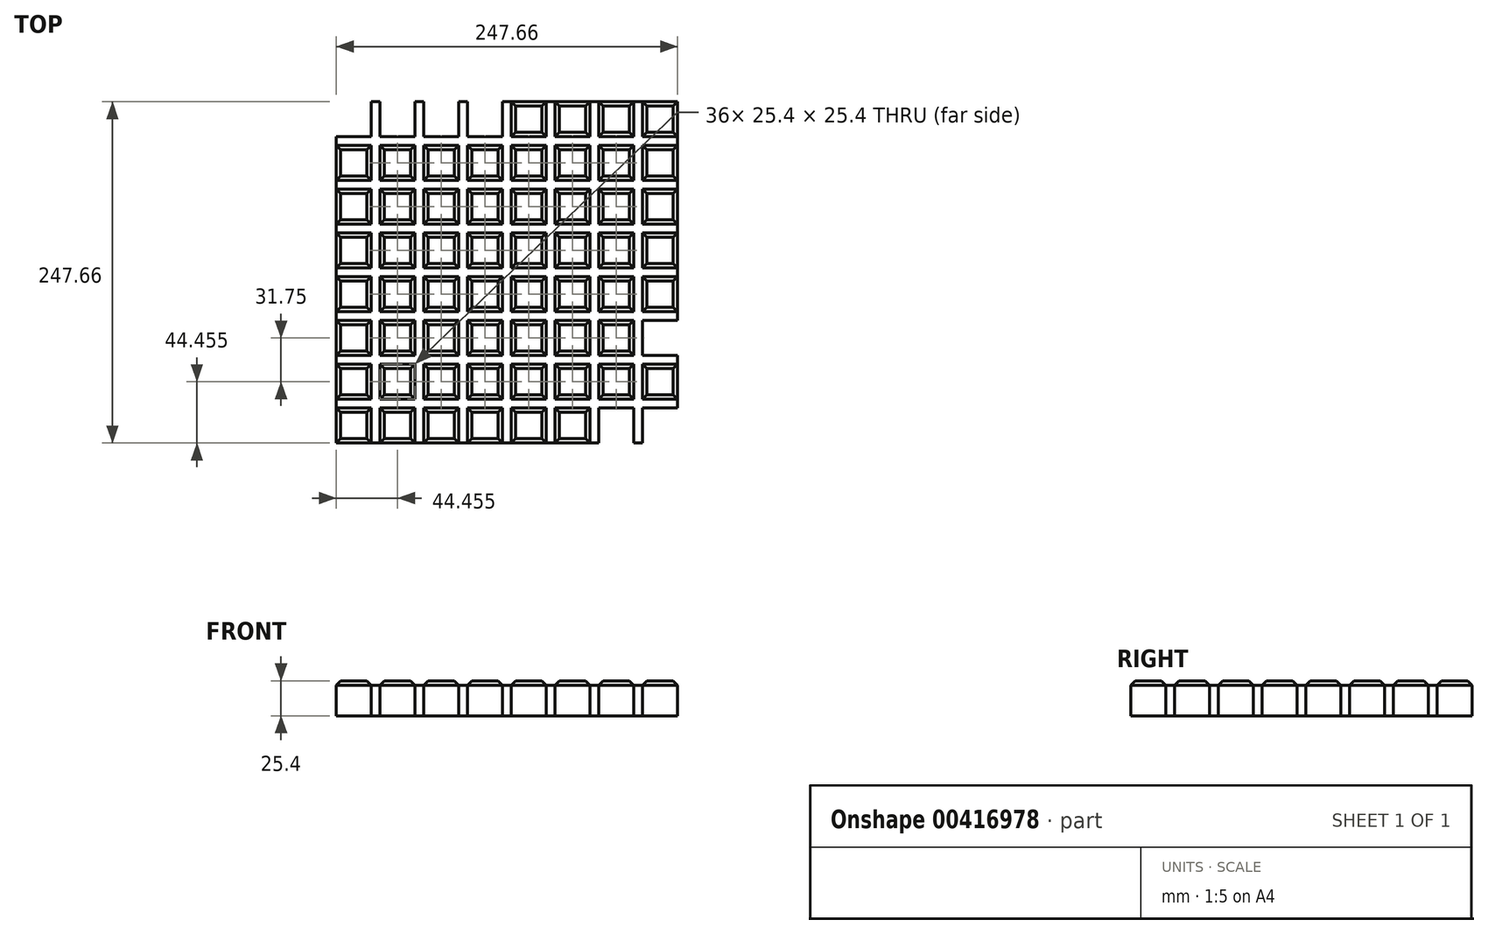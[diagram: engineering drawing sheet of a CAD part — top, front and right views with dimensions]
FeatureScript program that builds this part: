
annotation { "Feature Type Name" : "Feature", "Feature Type Description" : "" }
export const myFeature = defineFeature(function(context is Context, id is Id, definition is map)
    precondition{}
    {
        {
            var Q0;
            Q0=qCreatedBy(makeId("Top.planeOp"),FACE);
            var sketch = newSketch(context, id + "F0", { "sketchPlane" : qUnion([Q0])});
            skLineSegment(sketch, "E0.bottom", {"start": v(123.83, 123.83) * mm, "end": v(-123.83, 123.83) * mm});
            skLineSegment(sketch, "E0.top", {"start": v(123.83, -123.83) * mm, "end": v(-123.83, -123.83) * mm});
            skLineSegment(sketch, "E0.left", {"start": v(123.83, 123.83) * mm, "end": v(123.83, -123.83) * mm});
            skLineSegment(sketch, "E0.right", {"start": v(-123.83, 123.82) * mm, "end": v(-123.83, -123.82) * mm});
            skLineSegment(sketch, "E1.bottom", {"start": v(-123.83, 123.83) * mm, "end": v(-98.43, 123.83) * mm});
            skLineSegment(sketch, "E1.top", {"start": v(-123.83, 98.43) * mm, "end": v(-98.43, 98.43) * mm});
            skLineSegment(sketch, "E1.left", {"start": v(-123.83, 123.83) * mm, "end": v(-123.83, 98.43) * mm});
            skLineSegment(sketch, "E1.right", {"start": v(-98.43, 123.83) * mm, "end": v(-98.43, 98.43) * mm});
            skLineSegment(sketch, "E2.bottom", {"start": v(-123.83, 92.08) * mm, "end": v(-98.43, 92.08) * mm});
            skLineSegment(sketch, "E2.top", {"start": v(-123.83, 66.68) * mm, "end": v(-98.43, 66.68) * mm});
            skLineSegment(sketch, "E2.left", {"start": v(-123.83, 92.08) * mm, "end": v(-123.83, 66.68) * mm});
            skLineSegment(sketch, "E2.right", {"start": v(-98.43, 92.08) * mm, "end": v(-98.43, 66.68) * mm});
            skLineSegment(sketch, "E3.bottom", {"start": v(-92.08, 123.83) * mm, "end": v(-66.68, 123.83) * mm});
            skLineSegment(sketch, "E3.top", {"start": v(-92.08, 98.43) * mm, "end": v(-66.68, 98.43) * mm});
            skLineSegment(sketch, "E3.left", {"start": v(-92.08, 123.83) * mm, "end": v(-92.08, 98.43) * mm});
            skLineSegment(sketch, "E3.right", {"start": v(-66.68, 123.83) * mm, "end": v(-66.68, 98.43) * mm});
            skLineSegment(sketch, "E4.bottom", {"start": v(-123.83, 60.33) * mm, "end": v(-98.43, 60.33) * mm});
            skLineSegment(sketch, "E4.top", {"start": v(-123.83, 34.92) * mm, "end": v(-98.43, 34.92) * mm});
            skLineSegment(sketch, "E4.left", {"start": v(-123.83, 60.33) * mm, "end": v(-123.83, 34.92) * mm});
            skLineSegment(sketch, "E4.right", {"start": v(-98.43, 60.33) * mm, "end": v(-98.43, 34.92) * mm});
            skLineSegment(sketch, "E5.bottom", {"start": v(-60.33, 123.83) * mm, "end": v(-34.93, 123.83) * mm});
            skLineSegment(sketch, "E5.top", {"start": v(-60.33, 98.43) * mm, "end": v(-34.93, 98.43) * mm});
            skLineSegment(sketch, "E5.left", {"start": v(-60.33, 123.83) * mm, "end": v(-60.33, 98.43) * mm});
            skLineSegment(sketch, "E5.right", {"start": v(-34.93, 123.83) * mm, "end": v(-34.93, 98.43) * mm});
            skLineSegment(sketch, "E6.bottom", {"start": v(-92.08, 92.08) * mm, "end": v(-66.68, 92.08) * mm});
            skLineSegment(sketch, "E6.top", {"start": v(-92.08, 66.68) * mm, "end": v(-66.68, 66.68) * mm});
            skLineSegment(sketch, "E6.left", {"start": v(-92.08, 92.08) * mm, "end": v(-92.08, 66.68) * mm});
            skLineSegment(sketch, "E6.right", {"start": v(-66.68, 92.08) * mm, "end": v(-66.68, 66.68) * mm});
            skLineSegment(sketch, "E7.bottom", {"start": v(-92.08, 60.33) * mm, "end": v(-66.68, 60.33) * mm});
            skLineSegment(sketch, "E7.top", {"start": v(-92.08, 34.93) * mm, "end": v(-66.68, 34.93) * mm});
            skLineSegment(sketch, "E7.left", {"start": v(-92.08, 60.33) * mm, "end": v(-92.08, 34.93) * mm});
            skLineSegment(sketch, "E7.right", {"start": v(-66.68, 60.33) * mm, "end": v(-66.68, 34.93) * mm});
            skLineSegment(sketch, "E8.bottom", {"start": v(-60.33, 92.08) * mm, "end": v(-34.93, 92.08) * mm});
            skLineSegment(sketch, "E8.top", {"start": v(-60.33, 66.68) * mm, "end": v(-34.93, 66.68) * mm});
            skLineSegment(sketch, "E8.left", {"start": v(-60.33, 92.08) * mm, "end": v(-60.33, 66.68) * mm});
            skLineSegment(sketch, "E8.right", {"start": v(-34.93, 92.08) * mm, "end": v(-34.93, 66.68) * mm});
            skLineSegment(sketch, "E9.bottom", {"start": v(-60.33, 60.33) * mm, "end": v(-34.93, 60.33) * mm});
            skLineSegment(sketch, "E9.top", {"start": v(-60.33, 34.93) * mm, "end": v(-34.93, 34.93) * mm});
            skLineSegment(sketch, "E9.left", {"start": v(-60.33, 60.33) * mm, "end": v(-60.33, 34.93) * mm});
            skLineSegment(sketch, "E9.right", {"start": v(-34.93, 60.33) * mm, "end": v(-34.93, 34.93) * mm});
            skLineSegment(sketch, "E10.bottom", {"start": v(-60.33, 28.58) * mm, "end": v(-34.93, 28.58) * mm});
            skLineSegment(sketch, "E10.top", {"start": v(-60.33, 3.18) * mm, "end": v(-34.93, 3.18) * mm});
            skLineSegment(sketch, "E10.left", {"start": v(-60.33, 28.58) * mm, "end": v(-60.33, 3.18) * mm});
            skLineSegment(sketch, "E10.right", {"start": v(-34.93, 28.58) * mm, "end": v(-34.93, 3.18) * mm});
            skLineSegment(sketch, "E11.bottom", {"start": v(-92.08, 28.58) * mm, "end": v(-66.68, 28.58) * mm});
            skLineSegment(sketch, "E11.top", {"start": v(-92.08, 3.18) * mm, "end": v(-66.68, 3.18) * mm});
            skLineSegment(sketch, "E11.left", {"start": v(-92.08, 28.58) * mm, "end": v(-92.08, 3.18) * mm});
            skLineSegment(sketch, "E11.right", {"start": v(-66.68, 28.58) * mm, "end": v(-66.68, 3.18) * mm});
            skLineSegment(sketch, "E12.bottom", {"start": v(-123.83, 28.58) * mm, "end": v(-98.43, 28.58) * mm});
            skLineSegment(sketch, "E12.top", {"start": v(-123.83, 3.18) * mm, "end": v(-98.43, 3.18) * mm});
            skLineSegment(sketch, "E12.left", {"start": v(-123.83, 28.58) * mm, "end": v(-123.83, 3.18) * mm});
            skLineSegment(sketch, "E12.right", {"start": v(-98.43, 28.58) * mm, "end": v(-98.43, 3.18) * mm});
            skLineSegment(sketch, "E13.bottom", {"start": v(-28.58, 123.83) * mm, "end": v(-3.18, 123.83) * mm});
            skLineSegment(sketch, "E13.top", {"start": v(-28.58, 98.43) * mm, "end": v(-3.18, 98.43) * mm});
            skLineSegment(sketch, "E13.left", {"start": v(-28.58, 123.83) * mm, "end": v(-28.58, 98.42) * mm});
            skLineSegment(sketch, "E13.right", {"start": v(-3.18, 123.83) * mm, "end": v(-3.18, 98.42) * mm});
            skLineSegment(sketch, "E14.bottom", {"start": v(-28.58, 92.07) * mm, "end": v(-3.18, 92.07) * mm});
            skLineSegment(sketch, "E14.top", {"start": v(-28.58, 66.67) * mm, "end": v(-3.18, 66.67) * mm});
            skLineSegment(sketch, "E14.left", {"start": v(-28.58, 92.07) * mm, "end": v(-28.58, 66.67) * mm});
            skLineSegment(sketch, "E14.right", {"start": v(-3.18, 92.08) * mm, "end": v(-3.18, 66.67) * mm});
            skLineSegment(sketch, "E15.bottom", {"start": v(-28.58, 60.32) * mm, "end": v(-3.18, 60.32) * mm});
            skLineSegment(sketch, "E15.top", {"start": v(-28.58, 34.92) * mm, "end": v(-3.18, 34.92) * mm});
            skLineSegment(sketch, "E15.left", {"start": v(-28.58, 60.32) * mm, "end": v(-28.58, 34.92) * mm});
            skLineSegment(sketch, "E15.right", {"start": v(-3.18, 60.32) * mm, "end": v(-3.18, 34.92) * mm});
            skLineSegment(sketch, "E16.bottom", {"start": v(-28.58, 28.57) * mm, "end": v(-3.18, 28.57) * mm});
            skLineSegment(sketch, "E16.top", {"start": v(-28.58, 3.17) * mm, "end": v(-3.18, 3.17) * mm});
            skLineSegment(sketch, "E16.left", {"start": v(-28.58, 28.57) * mm, "end": v(-28.58, 3.17) * mm});
            skLineSegment(sketch, "E16.right", {"start": v(-3.18, 28.57) * mm, "end": v(-3.18, 3.17) * mm});
            skLineSegment(sketch, "E17.MirrorCS", {"start": v(28.57, 60.32) * mm, "end": v(28.57, 34.92) * mm});
            skLineSegment(sketch, "E18.MirrorCS", {"start": v(60.33, 34.93) * mm, "end": v(34.93, 34.93) * mm});
            skLineSegment(sketch, "E19.MirrorCS", {"start": v(60.32, 60.33) * mm, "end": v(60.32, 34.93) * mm});
            skLineSegment(sketch, "E20.MirrorCS", {"start": v(60.33, 28.58) * mm, "end": v(34.93, 28.58) * mm});
            skLineSegment(sketch, "E21.MirrorCS", {"start": v(92.08, 98.43) * mm, "end": v(66.68, 98.43) * mm});
            skLineSegment(sketch, "E22.MirrorCS", {"start": v(66.67, 28.57) * mm, "end": v(66.67, 3.17) * mm});
            skLineSegment(sketch, "E23.MirrorCS", {"start": v(28.58, 60.33) * mm, "end": v(3.18, 60.33) * mm});
            skLineSegment(sketch, "E24.MirrorCS", {"start": v(60.32, 28.58) * mm, "end": v(60.33, 3.17) * mm});
            skLineSegment(sketch, "E25.MirrorCS", {"start": v(92.08, 28.58) * mm, "end": v(66.68, 28.58) * mm});
            skLineSegment(sketch, "E26.MirrorCS", {"start": v(98.42, 92.08) * mm, "end": v(98.42, 66.67) * mm});
            skLineSegment(sketch, "E27.MirrorCS", {"start": v(92.08, 92.08) * mm, "end": v(66.68, 92.08) * mm});
            skLineSegment(sketch, "E28.MirrorCS", {"start": v(92.07, 28.57) * mm, "end": v(92.08, 3.17) * mm});
            skLineSegment(sketch, "E29.MirrorCS", {"start": v(98.42, 60.32) * mm, "end": v(98.42, 34.92) * mm});
            skLineSegment(sketch, "E30.MirrorCS", {"start": v(34.92, 60.33) * mm, "end": v(34.92, 34.93) * mm});
            skLineSegment(sketch, "E31.MirrorCS", {"start": v(98.42, 28.57) * mm, "end": v(98.42, 3.17) * mm});
            skLineSegment(sketch, "E32.MirrorCS", {"start": v(28.57, 92.07) * mm, "end": v(28.57, 66.67) * mm});
            skLineSegment(sketch, "E33.MirrorCS", {"start": v(98.42, 123.83) * mm, "end": v(98.42, 98.43) * mm});
            skLineSegment(sketch, "E34.MirrorCS", {"start": v(123.83, 92.08) * mm, "end": v(98.43, 92.08) * mm});
            skLineSegment(sketch, "E35.MirrorCS", {"start": v(28.58, 28.58) * mm, "end": v(3.18, 28.58) * mm});
            skLineSegment(sketch, "E36.MirrorCS", {"start": v(92.07, 92.07) * mm, "end": v(92.07, 66.67) * mm});
            skLineSegment(sketch, "E37.MirrorCS", {"start": v(66.67, 92.08) * mm, "end": v(66.67, 66.68) * mm});
            skLineSegment(sketch, "E38.MirrorCS", {"start": v(92.07, 60.32) * mm, "end": v(92.07, 34.92) * mm});
            skLineSegment(sketch, "E39.MirrorCS", {"start": v(28.57, 123.83) * mm, "end": v(28.57, 98.42) * mm});
            skLineSegment(sketch, "E40.MirrorCS", {"start": v(66.67, 60.33) * mm, "end": v(66.67, 34.93) * mm});
            skLineSegment(sketch, "E41.MirrorCS", {"start": v(92.07, 123.82) * mm, "end": v(92.07, 98.42) * mm});
            skLineSegment(sketch, "E42.MirrorCS", {"start": v(28.58, 66.68) * mm, "end": v(3.18, 66.68) * mm});
            skLineSegment(sketch, "E43.MirrorCS", {"start": v(34.92, 92.08) * mm, "end": v(34.92, 66.68) * mm});
            skLineSegment(sketch, "E44.MirrorCS", {"start": v(60.32, 92.08) * mm, "end": v(60.32, 66.68) * mm});
            skLineSegment(sketch, "E45.MirrorCS", {"start": v(123.83, 98.43) * mm, "end": v(98.43, 98.43) * mm});
            skLineSegment(sketch, "E46.MirrorCS", {"start": v(28.58, 34.93) * mm, "end": v(3.18, 34.93) * mm});
            skLineSegment(sketch, "E47.MirrorCS", {"start": v(92.08, 34.93) * mm, "end": v(66.68, 34.93) * mm});
            skLineSegment(sketch, "E48.MirrorCS", {"start": v(34.92, 123.83) * mm, "end": v(34.92, 98.43) * mm});
            skLineSegment(sketch, "E49.MirrorCS", {"start": v(28.58, 28.57) * mm, "end": v(28.58, 3.17) * mm});
            skLineSegment(sketch, "E50.MirrorCS", {"start": v(123.83, 28.57) * mm, "end": v(123.83, 3.17) * mm});
            skLineSegment(sketch, "E51.MirrorCS", {"start": v(92.08, 60.33) * mm, "end": v(66.68, 60.33) * mm});
            skLineSegment(sketch, "E52.MirrorCS", {"start": v(60.33, 98.43) * mm, "end": v(34.93, 98.43) * mm});
            skLineSegment(sketch, "E53.MirrorCS", {"start": v(92.08, 66.68) * mm, "end": v(66.68, 66.68) * mm});
            skLineSegment(sketch, "E54.MirrorCS", {"start": v(3.17, 60.32) * mm, "end": v(3.17, 34.92) * mm});
            skLineSegment(sketch, "E55.MirrorCS", {"start": v(92.08, 123.83) * mm, "end": v(66.68, 123.83) * mm});
            skLineSegment(sketch, "E56.MirrorCS", {"start": v(28.58, 98.43) * mm, "end": v(3.18, 98.43) * mm});
            skLineSegment(sketch, "E57.MirrorCS", {"start": v(123.82, 60.32) * mm, "end": v(123.82, 34.92) * mm});
            skLineSegment(sketch, "E58.MirrorCS", {"start": v(28.58, 3.18) * mm, "end": v(3.18, 3.18) * mm});
            skLineSegment(sketch, "E59.MirrorCS", {"start": v(123.83, 66.68) * mm, "end": v(98.43, 66.68) * mm});
            skLineSegment(sketch, "E60.MirrorCS", {"start": v(123.83, 28.58) * mm, "end": v(98.43, 28.58) * mm});
            skLineSegment(sketch, "E61.MirrorCS", {"start": v(60.33, 66.68) * mm, "end": v(34.93, 66.68) * mm});
            skLineSegment(sketch, "E62.MirrorCS", {"start": v(60.33, 92.08) * mm, "end": v(34.93, 92.08) * mm});
            skLineSegment(sketch, "E63.MirrorCS", {"start": v(28.58, 123.83) * mm, "end": v(3.18, 123.83) * mm});
            skLineSegment(sketch, "E64.MirrorCS", {"start": v(92.08, 3.18) * mm, "end": v(66.68, 3.18) * mm});
            skLineSegment(sketch, "E65.MirrorCS", {"start": v(60.33, 3.18) * mm, "end": v(34.93, 3.18) * mm});
            skLineSegment(sketch, "E66.MirrorCS", {"start": v(28.58, 92.08) * mm, "end": v(3.18, 92.08) * mm});
            skLineSegment(sketch, "E67.MirrorCS", {"start": v(60.32, 123.83) * mm, "end": v(60.32, 98.43) * mm});
            skLineSegment(sketch, "E68.MirrorCS", {"start": v(66.67, 123.82) * mm, "end": v(66.67, 98.43) * mm});
            skLineSegment(sketch, "E69.MirrorCS", {"start": v(123.83, 123.83) * mm, "end": v(98.43, 123.83) * mm});
            skLineSegment(sketch, "E70.MirrorCS", {"start": v(3.18, 28.57) * mm, "end": v(3.18, 3.17) * mm});
            skLineSegment(sketch, "E71.MirrorCS", {"start": v(34.93, 28.58) * mm, "end": v(34.93, 3.18) * mm});
            skLineSegment(sketch, "E72.MirrorCS", {"start": v(3.17, 92.08) * mm, "end": v(3.17, 66.67) * mm});
            skLineSegment(sketch, "E73.MirrorCS", {"start": v(123.83, 123.82) * mm, "end": v(123.83, 98.42) * mm});
            skLineSegment(sketch, "E74.MirrorCS", {"start": v(123.83, 34.93) * mm, "end": v(98.43, 34.93) * mm});
            skLineSegment(sketch, "E75.MirrorCS", {"start": v(60.33, 123.83) * mm, "end": v(34.93, 123.83) * mm});
            skLineSegment(sketch, "E76.MirrorCS", {"start": v(123.82, 92.07) * mm, "end": v(123.82, 66.67) * mm});
            skLineSegment(sketch, "E77.MirrorCS", {"start": v(60.33, 60.33) * mm, "end": v(34.93, 60.33) * mm});
            skLineSegment(sketch, "E78.MirrorCS", {"start": v(123.83, 3.18) * mm, "end": v(98.43, 3.18) * mm});
            skLineSegment(sketch, "E79.MirrorCS", {"start": v(3.17, 123.83) * mm, "end": v(3.17, 98.42) * mm});
            skLineSegment(sketch, "E80.MirrorCS", {"start": v(123.83, 60.33) * mm, "end": v(98.43, 60.33) * mm});
            skLineSegment(sketch, "E81.MirrorCS", {"start": v(-60.32, -60.33) * mm, "end": v(-60.32, -34.93) * mm});
            skLineSegment(sketch, "E82.MirrorCS", {"start": v(-92.08, -28.58) * mm, "end": v(-66.68, -28.58) * mm});
            skLineSegment(sketch, "E83.MirrorCS", {"start": v(-92.08, -60.33) * mm, "end": v(-66.68, -60.33) * mm});
            skLineSegment(sketch, "E84.MirrorCS", {"start": v(-92.07, -92.08) * mm, "end": v(-92.07, -66.68) * mm});
            skLineSegment(sketch, "E85.MirrorCS", {"start": v(-28.58, -28.57) * mm, "end": v(-3.18, -28.57) * mm});
            skLineSegment(sketch, "E86.MirrorCS", {"start": v(-123.83, -60.33) * mm, "end": v(-98.43, -60.33) * mm});
            skLineSegment(sketch, "E87.MirrorCS", {"start": v(-28.58, -60.33) * mm, "end": v(-3.18, -60.33) * mm});
            skLineSegment(sketch, "E88.MirrorCS", {"start": v(-123.83, -66.68) * mm, "end": v(-98.43, -66.68) * mm});
            skLineSegment(sketch, "E89.MirrorCS", {"start": v(-60.33, -34.93) * mm, "end": v(-34.93, -34.93) * mm});
            skLineSegment(sketch, "E90.MirrorCS", {"start": v(-60.33, -92.08) * mm, "end": v(-34.93, -92.08) * mm});
            skLineSegment(sketch, "E91.MirrorCS", {"start": v(-60.32, -92.08) * mm, "end": v(-60.32, -66.68) * mm});
            skLineSegment(sketch, "E92.MirrorCS", {"start": v(-28.58, -98.43) * mm, "end": v(-3.17, -98.43) * mm});
            skLineSegment(sketch, "E93.MirrorCS", {"start": v(-28.57, -123.83) * mm, "end": v(-28.57, -98.42) * mm});
            skLineSegment(sketch, "E94.MirrorCS", {"start": v(-98.42, -123.83) * mm, "end": v(-98.42, -98.43) * mm});
            skLineSegment(sketch, "E95.MirrorCS", {"start": v(-123.83, -92.08) * mm, "end": v(-98.43, -92.08) * mm});
            skLineSegment(sketch, "E96.MirrorCS", {"start": v(-60.33, -98.43) * mm, "end": v(-34.93, -98.43) * mm});
            skLineSegment(sketch, "E97.MirrorCS", {"start": v(3.18, -123.83) * mm, "end": v(3.18, -98.42) * mm});
            skLineSegment(sketch, "E98.MirrorCS", {"start": v(-66.67, -92.08) * mm, "end": v(-66.67, -66.68) * mm});
            skLineSegment(sketch, "E99.MirrorCS", {"start": v(-60.33, -28.58) * mm, "end": v(-34.93, -28.58) * mm});
            skLineSegment(sketch, "E100.MirrorCS", {"start": v(-28.58, -92.08) * mm, "end": v(-3.18, -92.08) * mm});
            skLineSegment(sketch, "E101.MirrorCS", {"start": v(-98.43, -92.08) * mm, "end": v(-98.43, -66.68) * mm});
            skLineSegment(sketch, "E102.MirrorCS", {"start": v(-123.83, -98.43) * mm, "end": v(-98.43, -98.43) * mm});
            skLineSegment(sketch, "E103.MirrorCS", {"start": v(-98.42, -28.58) * mm, "end": v(-98.43, -3.18) * mm});
            skLineSegment(sketch, "E104.MirrorCS", {"start": v(-92.07, -123.83) * mm, "end": v(-92.07, -98.43) * mm});
            skLineSegment(sketch, "E105.MirrorCS", {"start": v(-92.08, -98.43) * mm, "end": v(-66.68, -98.43) * mm});
            skLineSegment(sketch, "E106.MirrorCS", {"start": v(-28.58, -66.68) * mm, "end": v(-3.17, -66.68) * mm});
            skLineSegment(sketch, "E107.MirrorCS", {"start": v(-66.67, -60.33) * mm, "end": v(-66.67, -34.93) * mm});
            skLineSegment(sketch, "E108.MirrorCS", {"start": v(-66.67, -28.58) * mm, "end": v(-66.68, -3.18) * mm});
            skLineSegment(sketch, "E109.MirrorCS", {"start": v(-92.08, -92.08) * mm, "end": v(-66.68, -92.08) * mm});
            skLineSegment(sketch, "E110.MirrorCS", {"start": v(-92.08, -34.93) * mm, "end": v(-66.68, -34.93) * mm});
            skLineSegment(sketch, "E111.MirrorCS", {"start": v(-28.58, -34.93) * mm, "end": v(-3.18, -34.93) * mm});
            skLineSegment(sketch, "E112.MirrorCS", {"start": v(-34.92, -92.08) * mm, "end": v(-34.92, -66.68) * mm});
            skLineSegment(sketch, "E113.MirrorCS", {"start": v(-34.92, -123.83) * mm, "end": v(-34.92, -98.43) * mm});
            skLineSegment(sketch, "E114.MirrorCS", {"start": v(-34.92, -60.33) * mm, "end": v(-34.92, -34.93) * mm});
            skLineSegment(sketch, "E115.MirrorCS", {"start": v(-3.17, -123.83) * mm, "end": v(-3.17, -98.42) * mm});
            skLineSegment(sketch, "E116.MirrorCS", {"start": v(-60.32, -28.58) * mm, "end": v(-60.33, -3.18) * mm});
            skLineSegment(sketch, "E117.MirrorCS", {"start": v(-28.57, -92.07) * mm, "end": v(-28.57, -66.67) * mm});
            skLineSegment(sketch, "E118.MirrorCS", {"start": v(-98.43, -60.33) * mm, "end": v(-98.43, -34.93) * mm});
            skLineSegment(sketch, "E119.MirrorCS", {"start": v(-28.57, -60.32) * mm, "end": v(-28.57, -34.92) * mm});
            skLineSegment(sketch, "E120.MirrorCS", {"start": v(-92.07, -28.58) * mm, "end": v(-92.08, -3.18) * mm});
            skLineSegment(sketch, "E121.MirrorCS", {"start": v(-92.07, -60.33) * mm, "end": v(-92.07, -34.93) * mm});
            skLineSegment(sketch, "E122.MirrorCS", {"start": v(28.58, -28.57) * mm, "end": v(28.58, -3.17) * mm});
            skLineSegment(sketch, "E123.MirrorCS", {"start": v(28.58, -28.58) * mm, "end": v(3.18, -28.58) * mm});
            skLineSegment(sketch, "E124.MirrorCS", {"start": v(-123.83, -92.08) * mm, "end": v(-123.83, -66.68) * mm});
            skLineSegment(sketch, "E125.MirrorCS", {"start": v(-92.08, -66.68) * mm, "end": v(-66.68, -66.68) * mm});
            skLineSegment(sketch, "E126.MirrorCS", {"start": v(-28.57, -123.83) * mm, "end": v(-3.17, -123.83) * mm});
            skLineSegment(sketch, "E127.MirrorCS", {"start": v(28.58, -60.33) * mm, "end": v(3.18, -60.33) * mm});
            skLineSegment(sketch, "E128.MirrorCS", {"start": v(-123.83, -60.33) * mm, "end": v(-123.83, -34.93) * mm});
            skLineSegment(sketch, "E129.MirrorCS", {"start": v(28.58, -123.83) * mm, "end": v(28.58, -98.42) * mm});
            skLineSegment(sketch, "E130.MirrorCS", {"start": v(-123.83, -28.58) * mm, "end": v(-98.43, -28.58) * mm});
            skLineSegment(sketch, "E131.MirrorCS", {"start": v(-123.83, -34.93) * mm, "end": v(-98.43, -34.93) * mm});
            skLineSegment(sketch, "E132.MirrorCS", {"start": v(-60.32, -123.83) * mm, "end": v(-60.32, -98.43) * mm});
            skLineSegment(sketch, "E133.MirrorCS", {"start": v(-60.33, -123.83) * mm, "end": v(-34.93, -123.83) * mm});
            skLineSegment(sketch, "E134.MirrorCS", {"start": v(3.18, -60.32) * mm, "end": v(3.18, -34.92) * mm});
            skLineSegment(sketch, "E135.MirrorCS", {"start": v(28.58, -123.83) * mm, "end": v(3.18, -123.83) * mm});
            skLineSegment(sketch, "E136.MirrorCS", {"start": v(-123.83, -28.58) * mm, "end": v(-123.83, -3.18) * mm});
            skLineSegment(sketch, "E137.MirrorCS", {"start": v(28.58, -60.32) * mm, "end": v(28.58, -34.92) * mm});
            skLineSegment(sketch, "E138.MirrorCS", {"start": v(-92.08, -123.83) * mm, "end": v(-66.68, -123.83) * mm});
            skLineSegment(sketch, "E139.MirrorCS", {"start": v(-28.57, -28.57) * mm, "end": v(-28.58, -3.17) * mm});
            skLineSegment(sketch, "E140.MirrorCS", {"start": v(-60.33, -66.68) * mm, "end": v(-34.93, -66.68) * mm});
            skLineSegment(sketch, "E141.MirrorCS", {"start": v(28.58, -34.93) * mm, "end": v(3.18, -34.93) * mm});
            skLineSegment(sketch, "E142.MirrorCS", {"start": v(-3.17, -92.08) * mm, "end": v(-3.17, -66.67) * mm});
            skLineSegment(sketch, "E143.MirrorCS", {"start": v(-123.83, -123.83) * mm, "end": v(-123.83, -98.43) * mm});
            skLineSegment(sketch, "E144.MirrorCS", {"start": v(-123.83, -3.18) * mm, "end": v(-98.43, -3.18) * mm});
            skLineSegment(sketch, "E145.MirrorCS", {"start": v(-28.58, -3.17) * mm, "end": v(-3.18, -3.17) * mm});
            skLineSegment(sketch, "E146.MirrorCS", {"start": v(-123.83, -123.83) * mm, "end": v(-98.43, -123.83) * mm});
            skLineSegment(sketch, "E147.MirrorCS", {"start": v(-66.67, -123.83) * mm, "end": v(-66.67, -98.43) * mm});
            skLineSegment(sketch, "E148.MirrorCS", {"start": v(28.58, -66.67) * mm, "end": v(3.18, -66.68) * mm});
            skLineSegment(sketch, "E149.MirrorCS", {"start": v(28.58, -3.18) * mm, "end": v(3.18, -3.18) * mm});
            skLineSegment(sketch, "E150.MirrorCS", {"start": v(-3.17, -60.32) * mm, "end": v(-3.17, -34.92) * mm});
            skLineSegment(sketch, "E151.MirrorCS", {"start": v(-60.33, -3.18) * mm, "end": v(-34.93, -3.18) * mm});
            skLineSegment(sketch, "E152.MirrorCS", {"start": v(28.58, -92.07) * mm, "end": v(28.58, -66.67) * mm});
            skLineSegment(sketch, "E153.MirrorCS", {"start": v(-92.08, -3.18) * mm, "end": v(-66.68, -3.18) * mm});
            skLineSegment(sketch, "E154.MirrorCS", {"start": v(3.18, -28.57) * mm, "end": v(3.18, -3.17) * mm});
            skLineSegment(sketch, "E155.MirrorCS", {"start": v(-34.93, -28.58) * mm, "end": v(-34.93, -3.18) * mm});
            skLineSegment(sketch, "E156.MirrorCS", {"start": v(-60.33, -60.33) * mm, "end": v(-34.93, -60.33) * mm});
            skLineSegment(sketch, "E157.MirrorCS", {"start": v(28.58, -92.08) * mm, "end": v(3.18, -92.08) * mm});
            skLineSegment(sketch, "E158.MirrorCS", {"start": v(3.18, -92.08) * mm, "end": v(3.18, -66.67) * mm});
            skLineSegment(sketch, "E159.MirrorCS", {"start": v(-3.17, -28.57) * mm, "end": v(-3.18, -3.17) * mm});
            skLineSegment(sketch, "E160.MirrorCS", {"start": v(28.58, -98.42) * mm, "end": v(3.18, -98.43) * mm});
            skLineSegment(sketch, "E161.MirrorCS", {"start": v(66.68, -60.33) * mm, "end": v(66.68, -34.92) * mm});
            skLineSegment(sketch, "E162.MirrorCS", {"start": v(60.33, -92.08) * mm, "end": v(34.93, -92.08) * mm});
            skLineSegment(sketch, "E163.MirrorCS", {"start": v(92.08, -60.32) * mm, "end": v(92.08, -34.92) * mm});
            skLineSegment(sketch, "E164.MirrorCS", {"start": v(92.08, -123.83) * mm, "end": v(66.68, -123.83) * mm});
            skLineSegment(sketch, "E165.MirrorCS", {"start": v(123.83, -3.17) * mm, "end": v(98.43, -3.17) * mm});
            skLineSegment(sketch, "E166.MirrorCS", {"start": v(92.08, -28.57) * mm, "end": v(66.68, -28.57) * mm});
            skLineSegment(sketch, "E167.MirrorCS", {"start": v(92.08, -123.82) * mm, "end": v(92.08, -98.42) * mm});
            skLineSegment(sketch, "E168.MirrorCS", {"start": v(123.83, -60.32) * mm, "end": v(123.83, -34.92) * mm});
            skLineSegment(sketch, "E169.MirrorCS", {"start": v(66.68, -28.57) * mm, "end": v(66.68, -3.17) * mm});
            skLineSegment(sketch, "E170.MirrorCS", {"start": v(34.93, -28.58) * mm, "end": v(34.93, -3.18) * mm});
            skLineSegment(sketch, "E171.MirrorCS", {"start": v(123.83, -123.82) * mm, "end": v(123.83, -98.42) * mm});
            skLineSegment(sketch, "E172.MirrorCS", {"start": v(123.83, -92.07) * mm, "end": v(98.43, -92.07) * mm});
            skLineSegment(sketch, "E173.MirrorCS", {"start": v(92.08, -34.92) * mm, "end": v(66.68, -34.93) * mm});
            skLineSegment(sketch, "E174.MirrorCS", {"start": v(98.43, -28.57) * mm, "end": v(98.43, -3.17) * mm});
            skLineSegment(sketch, "E175.MirrorCS", {"start": v(34.93, -60.33) * mm, "end": v(34.93, -34.93) * mm});
            skLineSegment(sketch, "E176.MirrorCS", {"start": v(60.33, -98.42) * mm, "end": v(34.93, -98.42) * mm});
            skLineSegment(sketch, "E177.MirrorCS", {"start": v(92.08, -92.07) * mm, "end": v(92.08, -66.67) * mm});
            skLineSegment(sketch, "E178.MirrorCS", {"start": v(123.83, -60.32) * mm, "end": v(98.43, -60.32) * mm});
            skLineSegment(sketch, "E179.MirrorCS", {"start": v(92.08, -60.32) * mm, "end": v(66.68, -60.32) * mm});
            skLineSegment(sketch, "E180.MirrorCS", {"start": v(92.08, -3.17) * mm, "end": v(66.68, -3.17) * mm});
            skLineSegment(sketch, "E181.MirrorCS", {"start": v(34.93, -123.83) * mm, "end": v(34.93, -98.43) * mm});
            skLineSegment(sketch, "E182.MirrorCS", {"start": v(60.33, -28.58) * mm, "end": v(34.93, -28.58) * mm});
            skLineSegment(sketch, "E183.MirrorCS", {"start": v(98.43, -123.82) * mm, "end": v(98.43, -98.43) * mm});
            skLineSegment(sketch, "E184.MirrorCS", {"start": v(66.68, -123.82) * mm, "end": v(66.68, -98.42) * mm});
            skLineSegment(sketch, "E185.MirrorCS", {"start": v(123.83, -28.57) * mm, "end": v(123.83, -3.17) * mm});
            skLineSegment(sketch, "E186.MirrorCS", {"start": v(60.33, -34.93) * mm, "end": v(34.93, -34.93) * mm});
            skLineSegment(sketch, "E187.MirrorCS", {"start": v(123.83, -123.82) * mm, "end": v(98.43, -123.83) * mm});
            skLineSegment(sketch, "E188.MirrorCS", {"start": v(66.68, -92.08) * mm, "end": v(66.68, -66.68) * mm});
            skLineSegment(sketch, "E189.MirrorCS", {"start": v(92.08, -66.67) * mm, "end": v(66.68, -66.67) * mm});
            skLineSegment(sketch, "E190.MirrorCS", {"start": v(92.08, -98.42) * mm, "end": v(66.68, -98.42) * mm});
            skLineSegment(sketch, "E191.MirrorCS", {"start": v(60.33, -28.57) * mm, "end": v(60.33, -3.17) * mm});
            skLineSegment(sketch, "E192.MirrorCS", {"start": v(60.33, -123.83) * mm, "end": v(60.33, -98.43) * mm});
            skLineSegment(sketch, "E193.MirrorCS", {"start": v(60.33, -60.33) * mm, "end": v(60.33, -34.92) * mm});
            skLineSegment(sketch, "E194.MirrorCS", {"start": v(60.33, -3.17) * mm, "end": v(34.93, -3.17) * mm});
            skLineSegment(sketch, "E195.MirrorCS", {"start": v(98.43, -92.07) * mm, "end": v(98.43, -66.67) * mm});
            skLineSegment(sketch, "E196.MirrorCS", {"start": v(123.83, -34.92) * mm, "end": v(98.43, -34.92) * mm});
            skLineSegment(sketch, "E197.MirrorCS", {"start": v(60.33, -123.83) * mm, "end": v(34.93, -123.83) * mm});
            skLineSegment(sketch, "E198.MirrorCS", {"start": v(123.83, -66.67) * mm, "end": v(98.43, -66.67) * mm});
            skLineSegment(sketch, "E199.MirrorCS", {"start": v(34.93, -92.08) * mm, "end": v(34.93, -66.68) * mm});
            skLineSegment(sketch, "E200.MirrorCS", {"start": v(92.08, -92.07) * mm, "end": v(66.68, -92.08) * mm});
            skLineSegment(sketch, "E201.MirrorCS", {"start": v(92.08, -28.57) * mm, "end": v(92.08, -3.17) * mm});
            skLineSegment(sketch, "E202.MirrorCS", {"start": v(123.83, -92.07) * mm, "end": v(123.83, -66.67) * mm});
            skLineSegment(sketch, "E203.MirrorCS", {"start": v(123.83, -28.57) * mm, "end": v(98.43, -28.57) * mm});
            skLineSegment(sketch, "E204.MirrorCS", {"start": v(60.33, -92.08) * mm, "end": v(60.33, -66.68) * mm});
            skLineSegment(sketch, "E205.MirrorCS", {"start": v(98.43, -60.32) * mm, "end": v(98.43, -34.92) * mm});
            skLineSegment(sketch, "E206.MirrorCS", {"start": v(60.33, -60.33) * mm, "end": v(34.93, -60.33) * mm});
            skLineSegment(sketch, "E207.MirrorCS", {"start": v(123.83, -98.42) * mm, "end": v(98.43, -98.42) * mm});
            skLineSegment(sketch, "E208.MirrorCS", {"start": v(60.33, -66.68) * mm, "end": v(34.93, -66.68) * mm});
            skLineSegment(sketch, "E209.bottom", {"start": v(-130.17, 130.18) * mm, "end": v(130.18, 130.18) * mm});
            skLineSegment(sketch, "E209.top", {"start": v(-130.18, -130.18) * mm, "end": v(130.18, -130.18) * mm});
            skLineSegment(sketch, "E209.left", {"start": v(-130.17, 130.18) * mm, "end": v(-130.18, -130.18) * mm});
            skLineSegment(sketch, "E209.right", {"start": v(130.18, 130.18) * mm, "end": v(130.18, -130.18) * mm});
            skPoint(sketch, "E209.middle", {"position": v(0, 0) * mm});
            skSolve(sketch);
        }
        {
            var Q0;
            Q0=makeQuery(id+"F0.imprint","IMPRINT",FACE,{"disambiguationData":[TD([[makeQuery(id+"F0.imprint","IMPRINT",EDGE,{"derivedFrom":sQuery(id+"F0.wireOp",EDGE,"E32.MirrorCS")}),-1.0]])]});
            var Q1;
            Q1=makeQuery(id+"F0.imprint","IMPRINT",FACE,{"disambiguationData":[TD([[makeQuery(id+"F0.imprint","IMPRINT",EDGE,{"derivedFrom":sQuery(id+"F0.wireOp",EDGE,"E99.MirrorCS")}),1.0]])]});
            var Q2;
            Q2=makeQuery(id+"F0.imprint","IMPRINT",FACE,{"disambiguationData":[TD([[makeQuery(id+"F0.imprint","IMPRINT",EDGE,{"derivedFrom":sQuery(id+"F0.wireOp",EDGE,"E94.MirrorCS")}),1.0]])]});
            var Q3;
            Q3=makeQuery(id+"F0.imprint","IMPRINT",FACE,{"disambiguationData":[TD([[makeQuery(id+"F0.imprint","IMPRINT",EDGE,{"derivedFrom":sQuery(id+"F0.wireOp",EDGE,"E27.MirrorCS")}),1.0]])]});
            var Q4;
            Q4=makeQuery(id+"F0.imprint","IMPRINT",FACE,{"disambiguationData":[TD([[makeQuery(id+"F0.imprint","IMPRINT",EDGE,{"derivedFrom":sQuery(id+"F0.wireOp",EDGE,"E7.bottom")}),-1.0]])]});
            var Q5;
            Q5=makeQuery(id+"F0.imprint","IMPRINT",FACE,{"disambiguationData":[TD([[makeQuery(id+"F0.imprint","IMPRINT",EDGE,{"derivedFrom":sQuery(id+"F0.wireOp",EDGE,"E1.bottom")}),-1.0]])]});
            var Q6;
            Q6=makeQuery(id+"F0.imprint","IMPRINT",FACE,{"disambiguationData":[TD([[makeQuery(id+"F0.imprint","IMPRINT",EDGE,{"derivedFrom":sQuery(id+"F0.wireOp",EDGE,"E5.bottom")}),-1.0]])]});
            var Q7;
            Q7=makeQuery(id+"F0.imprint","IMPRINT",FACE,{"disambiguationData":[TD([[makeQuery(id+"F0.imprint","IMPRINT",EDGE,{"derivedFrom":sQuery(id+"F0.wireOp",EDGE,"E8.bottom")}),-1.0]])]});
            var Q8;
            Q8=makeQuery(id+"F0.imprint","IMPRINT",FACE,{"disambiguationData":[TD([[makeQuery(id+"F0.imprint","IMPRINT",EDGE,{"derivedFrom":sQuery(id+"F0.wireOp",EDGE,"E35.MirrorCS")}),1.0]])]});
            var Q9;
            Q9=makeQuery(id+"F0.imprint","IMPRINT",FACE,{"disambiguationData":[TD([[makeQuery(id+"F0.imprint","IMPRINT",EDGE,{"derivedFrom":sQuery(id+"F0.wireOp",EDGE,"E15.bottom")}),-1.0]])]});
            var Q10;
            Q10=makeQuery(id+"F0.imprint","IMPRINT",FACE,{"disambiguationData":[TD([[makeQuery(id+"F0.imprint","IMPRINT",EDGE,{"derivedFrom":sQuery(id+"F0.wireOp",EDGE,"E3.bottom")}),-1.0]])]});
            var Q11;
            Q11=makeQuery(id+"F0.imprint","IMPRINT",FACE,{"disambiguationData":[TD([[makeQuery(id+"F0.imprint","IMPRINT",EDGE,{"derivedFrom":sQuery(id+"F0.wireOp",EDGE,"E9.bottom")}),-1.0]])]});
            var Q12;
            Q12=makeQuery(id+"F0.imprint","IMPRINT",FACE,{"disambiguationData":[TD([[makeQuery(id+"F0.imprint","IMPRINT",EDGE,{"derivedFrom":sQuery(id+"F0.wireOp",EDGE,"E83.MirrorCS")}),1.0]])]});
            var Q13;
            Q13=makeQuery(id+"F0.imprint","IMPRINT",FACE,{"disambiguationData":[TD([[makeQuery(id+"F0.imprint","IMPRINT",EDGE,{"derivedFrom":sQuery(id+"F0.wireOp",EDGE,"E90.MirrorCS")}),1.0]])]});
            var Q14;
            Q14=makeQuery(id+"F0.imprint","IMPRINT",FACE,{"disambiguationData":[TD([[makeQuery(id+"F0.imprint","IMPRINT",EDGE,{"derivedFrom":sQuery(id+"F0.wireOp",EDGE,"E12.bottom")}),-1.0]])]});
            var Q15;
            Q15=makeQuery(id+"F0.imprint","IMPRINT",FACE,{"disambiguationData":[TD([[makeQuery(id+"F0.imprint","IMPRINT",EDGE,{"derivedFrom":sQuery(id+"F0.wireOp",EDGE,"E87.MirrorCS")}),1.0]])]});
            var Q16;
            Q16=makeQuery(id+"F0.imprint","IMPRINT",FACE,{"disambiguationData":[TD([[makeQuery(id+"F0.imprint","IMPRINT",EDGE,{"derivedFrom":sQuery(id+"F0.wireOp",EDGE,"E2.bottom")}),-1.0]])]});
            var Q17;
            Q17=makeQuery(id+"F0.imprint","IMPRINT",FACE,{"disambiguationData":[TD([[makeQuery(id+"F0.imprint","IMPRINT",EDGE,{"derivedFrom":sQuery(id+"F0.wireOp",EDGE,"E6.bottom")}),-1.0]])]});
            var Q18;
            Q18=makeQuery(id+"F0.imprint","IMPRINT",FACE,{"disambiguationData":[TD([[makeQuery(id+"F0.imprint","IMPRINT",EDGE,{"derivedFrom":sQuery(id+"F0.wireOp",EDGE,"E103.MirrorCS")}),1.0]])]});
            var Q19;
            Q19=makeQuery(id+"F0.imprint","IMPRINT",FACE,{"disambiguationData":[TD([[makeQuery(id+"F0.imprint","IMPRINT",EDGE,{"derivedFrom":sQuery(id+"F0.wireOp",EDGE,"E104.MirrorCS")}),-1.0]])]});
            var Q20;
            Q20=makeQuery(id+"F0.imprint","IMPRINT",FACE,{"disambiguationData":[TD([[makeQuery(id+"F0.imprint","IMPRINT",EDGE,{"derivedFrom":sQuery(id+"F0.wireOp",EDGE,"E85.MirrorCS")}),1.0]])]});
            var Q21;
            Q21=makeQuery(id+"F0.imprint","IMPRINT",FACE,{"disambiguationData":[TD([[makeQuery(id+"F0.imprint","IMPRINT",EDGE,{"derivedFrom":sQuery(id+"F0.wireOp",EDGE,"E92.MirrorCS")}),-1.0]])]});
            var Q22;
            Q22=makeQuery(id+"F0.imprint","IMPRINT",FACE,{"disambiguationData":[TD([[makeQuery(id+"F0.imprint","IMPRINT",EDGE,{"derivedFrom":sQuery(id+"F0.wireOp",EDGE,"E84.MirrorCS")}),-1.0]])]});
            var Q23;
            Q23=makeQuery(id+"F0.imprint","IMPRINT",FACE,{"disambiguationData":[TD([[makeQuery(id+"F0.imprint","IMPRINT",EDGE,{"derivedFrom":sQuery(id+"F0.wireOp",EDGE,"E96.MirrorCS")}),-1.0]])]});
            var Q24;
            Q24=makeQuery(id+"F0.imprint","IMPRINT",FACE,{"disambiguationData":[TD([[makeQuery(id+"F0.imprint","IMPRINT",EDGE,{"derivedFrom":sQuery(id+"F0.wireOp",EDGE,"E4.bottom")}),-1.0]])]});
            var Q25;
            Q25=makeQuery(id+"F0.imprint","IMPRINT",FACE,{"disambiguationData":[TD([[makeQuery(id+"F0.imprint","IMPRINT",EDGE,{"derivedFrom":sQuery(id+"F0.wireOp",EDGE,"E97.MirrorCS")}),-1.0]])]});
            var Q26;
            Q26=makeQuery(id+"F0.imprint","IMPRINT",FACE,{"disambiguationData":[TD([[makeQuery(id+"F0.imprint","IMPRINT",EDGE,{"derivedFrom":sQuery(id+"F0.wireOp",EDGE,"E38.MirrorCS")}),-1.0]])]});
            var Q27;
            Q27=makeQuery(id+"F0.imprint","IMPRINT",FACE,{"disambiguationData":[TD([[makeQuery(id+"F0.imprint","IMPRINT",EDGE,{"derivedFrom":sQuery(id+"F0.wireOp",EDGE,"E39.MirrorCS")}),-1.0]])]});
            var Q28;
            Q28=makeQuery(id+"F0.imprint","IMPRINT",FACE,{"disambiguationData":[TD([[makeQuery(id+"F0.imprint","IMPRINT",EDGE,{"derivedFrom":sQuery(id+"F0.wireOp",EDGE,"E22.MirrorCS")}),1.0]])]});
            var Q29;
            Q29=makeQuery(id+"F0.imprint","IMPRINT",FACE,{"disambiguationData":[TD([[makeQuery(id+"F0.imprint","IMPRINT",EDGE,{"derivedFrom":sQuery(id+"F0.wireOp",EDGE,"E20.MirrorCS")}),1.0]])]});
            var Q30;
            Q30=makeQuery(id+"F0.imprint","IMPRINT",FACE,{"disambiguationData":[TD([[makeQuery(id+"F0.imprint","IMPRINT",EDGE,{"derivedFrom":sQuery(id+"F0.wireOp",EDGE,"E166.MirrorCS")}),-1.0]])]});
            var Q31;
            Q31=makeQuery(id+"F0.imprint","IMPRINT",FACE,{"disambiguationData":[TD([[makeQuery(id+"F0.imprint","IMPRINT",EDGE,{"derivedFrom":sQuery(id+"F0.wireOp",EDGE,"E18.MirrorCS")}),-1.0]])]});
            var Q32;
            Q32=makeQuery(id+"F0.imprint","IMPRINT",FACE,{"disambiguationData":[TD([[makeQuery(id+"F0.imprint","IMPRINT",EDGE,{"derivedFrom":sQuery(id+"F0.wireOp",EDGE,"E17.MirrorCS")}),-1.0]])]});
            var Q33;
            Q33=makeQuery(id+"F0.imprint","IMPRINT",FACE,{"disambiguationData":[TD([[makeQuery(id+"F0.imprint","IMPRINT",EDGE,{"derivedFrom":sQuery(id+"F0.wireOp",EDGE,"E43.MirrorCS")}),1.0]])]});
            var Q34;
            Q34=makeQuery(id+"F0.imprint","IMPRINT",FACE,{"disambiguationData":[TD([[makeQuery(id+"F0.imprint","IMPRINT",EDGE,{"derivedFrom":sQuery(id+"F0.wireOp",EDGE,"E48.MirrorCS")}),1.0]])]});
            var Q35;
            Q35=makeQuery(id+"F0.imprint","IMPRINT",FACE,{"disambiguationData":[TD([[makeQuery(id+"F0.imprint","IMPRINT",EDGE,{"derivedFrom":sQuery(id+"F0.wireOp",EDGE,"E170.MirrorCS")}),-1.0]])]});
            var Q36;
            Q36=makeQuery(id+"F0.imprint","IMPRINT",FACE,{"disambiguationData":[TD([[makeQuery(id+"F0.imprint","IMPRINT",EDGE,{"derivedFrom":sQuery(id+"F0.wireOp",EDGE,"E16.bottom")}),-1.0]])]});
            var Q37;
            Q37=makeQuery(id+"F0.imprint","IMPRINT",FACE,{"disambiguationData":[TD([[makeQuery(id+"F0.imprint","IMPRINT",EDGE,{"derivedFrom":sQuery(id+"F0.wireOp",EDGE,"E164.MirrorCS")}),-1.0]])]});
            var Q38;
            Q38=makeQuery(id+"F0.imprint","IMPRINT",FACE,{"disambiguationData":[TD([[makeQuery(id+"F0.imprint","IMPRINT",EDGE,{"derivedFrom":sQuery(id+"F0.wireOp",EDGE,"E13.bottom")}),-1.0]])]});
            var Q39;
            Q39=makeQuery(id+"F0.imprint","IMPRINT",FACE,{"disambiguationData":[TD([[makeQuery(id+"F0.imprint","IMPRINT",EDGE,{"derivedFrom":sQuery(id+"F0.wireOp",EDGE,"E100.MirrorCS")}),1.0]])]});
            var Q40;
            Q40=makeQuery(id+"F0.imprint","IMPRINT",FACE,{"disambiguationData":[TD([[makeQuery(id+"F0.imprint","IMPRINT",EDGE,{"derivedFrom":sQuery(id+"F0.wireOp",EDGE,"E165.MirrorCS")}),1.0]])]});
            var Q41;
            Q41=makeQuery(id+"F0.imprint","IMPRINT",FACE,{"disambiguationData":[TD([[makeQuery(id+"F0.imprint","IMPRINT",EDGE,{"derivedFrom":sQuery(id+"F0.wireOp",EDGE,"E21.MirrorCS")}),-1.0]])]});
            var Q42;
            Q42=makeQuery(id+"F0.imprint","IMPRINT",FACE,{"disambiguationData":[TD([[makeQuery(id+"F0.imprint","IMPRINT",EDGE,{"derivedFrom":sQuery(id+"F0.wireOp",EDGE,"E11.bottom")}),-1.0]])]});
            var Q43;
            Q43=makeQuery(id+"F0.imprint","IMPRINT",FACE,{"disambiguationData":[TD([[makeQuery(id+"F0.imprint","IMPRINT",EDGE,{"derivedFrom":sQuery(id+"F0.wireOp",EDGE,"E122.MirrorCS")}),1.0]])]});
            var Q44;
            Q44=makeQuery(id+"F0.imprint","IMPRINT",FACE,{"disambiguationData":[TD([[makeQuery(id+"F0.imprint","IMPRINT",EDGE,{"derivedFrom":sQuery(id+"F0.wireOp",EDGE,"E168.MirrorCS")}),1.0]])]});
            var Q45;
            Q45=makeQuery(id+"F0.imprint","IMPRINT",FACE,{"disambiguationData":[TD([[makeQuery(id+"F0.imprint","IMPRINT",EDGE,{"derivedFrom":sQuery(id+"F0.wireOp",EDGE,"E26.MirrorCS")}),1.0]])]});
            var Q46;
            Q46=makeQuery(id+"F0.imprint","IMPRINT",FACE,{"disambiguationData":[TD([[makeQuery(id+"F0.imprint","IMPRINT",EDGE,{"derivedFrom":sQuery(id+"F0.wireOp",EDGE,"E127.MirrorCS")}),-1.0]])]});
            var Q47;
            Q47=makeQuery(id+"F0.imprint","IMPRINT",FACE,{"disambiguationData":[TD([[makeQuery(id+"F0.imprint","IMPRINT",EDGE,{"derivedFrom":sQuery(id+"F0.wireOp",EDGE,"E81.MirrorCS")}),-1.0]])]});
            var Q48;
            Q48=makeQuery(id+"F0.imprint","IMPRINT",FACE,{"disambiguationData":[TD([[makeQuery(id+"F0.imprint","IMPRINT",EDGE,{"derivedFrom":sQuery(id+"F0.wireOp",EDGE,"E175.MirrorCS")}),-1.0]])]});
            var Q49;
            Q49=makeQuery(id+"F0.imprint","IMPRINT",FACE,{"disambiguationData":[TD([[makeQuery(id+"F0.imprint","IMPRINT",EDGE,{"derivedFrom":sQuery(id+"F0.wireOp",EDGE,"E86.MirrorCS")}),1.0]])]});
            var Q50;
            Q50=makeQuery(id+"F0.imprint","IMPRINT",FACE,{"disambiguationData":[TD([[makeQuery(id+"F0.imprint","IMPRINT",EDGE,{"derivedFrom":sQuery(id+"F0.wireOp",EDGE,"E33.MirrorCS")}),1.0]])]});
            var Q51;
            Q51=makeQuery(id+"F0.imprint","IMPRINT",FACE,{"disambiguationData":[TD([[makeQuery(id+"F0.imprint","IMPRINT",EDGE,{"derivedFrom":sQuery(id+"F0.wireOp",EDGE,"E176.MirrorCS")}),1.0]])]});
            var Q52;
            Q52=makeQuery(id+"F0.imprint","IMPRINT",FACE,{"disambiguationData":[TD([[makeQuery(id+"F0.imprint","IMPRINT",EDGE,{"derivedFrom":sQuery(id+"F0.wireOp",EDGE,"E14.bottom")}),-1.0]])]});
            var Q53;
            Q53=makeQuery(id+"F0.imprint","IMPRINT",FACE,{"disambiguationData":[TD([[makeQuery(id+"F0.imprint","IMPRINT",EDGE,{"derivedFrom":sQuery(id+"F0.wireOp",EDGE,"E88.MirrorCS")}),-1.0]])]});
            var Q54;
            Q54=makeQuery(id+"F0.imprint","IMPRINT",FACE,{"disambiguationData":[TD([[makeQuery(id+"F0.imprint","IMPRINT",EDGE,{"derivedFrom":sQuery(id+"F0.wireOp",EDGE,"E177.MirrorCS")}),1.0]])]});
            var Q55;
            Q55=makeQuery(id+"F0.imprint","IMPRINT",FACE,{"disambiguationData":[TD([[makeQuery(id+"F0.imprint","IMPRINT",EDGE,{"derivedFrom":sQuery(id+"F0.wireOp",EDGE,"E171.MirrorCS")}),1.0]])]});
            var Q56;
            Q56=makeQuery(id+"F0.imprint","IMPRINT",FACE,{"disambiguationData":[TD([[makeQuery(id+"F0.imprint","IMPRINT",EDGE,{"derivedFrom":sQuery(id+"F0.wireOp",EDGE,"E29.MirrorCS")}),1.0]])]});
            var Q57;
            Q57=makeQuery(id+"F0.imprint","IMPRINT",FACE,{"disambiguationData":[TD([[makeQuery(id+"F0.imprint","IMPRINT",EDGE,{"derivedFrom":sQuery(id+"F0.wireOp",EDGE,"E148.MirrorCS")}),1.0]])]});
            var Q58;
            Q58=makeQuery(id+"F0.imprint","IMPRINT",FACE,{"disambiguationData":[TD([[makeQuery(id+"F0.imprint","IMPRINT",EDGE,{"derivedFrom":sQuery(id+"F0.wireOp",EDGE,"E82.MirrorCS")}),1.0]])]});
            var Q59;
            Q59=makeQuery(id+"F0.imprint","IMPRINT",FACE,{"disambiguationData":[TD([[makeQuery(id+"F0.imprint","IMPRINT",EDGE,{"derivedFrom":sQuery(id+"F0.wireOp",EDGE,"E162.MirrorCS")}),-1.0]])]});
            var Q60;
            Q60=makeQuery(id+"F0.imprint","IMPRINT",FACE,{"disambiguationData":[TD([[makeQuery(id+"F0.imprint","IMPRINT",EDGE,{"derivedFrom":sQuery(id+"F0.wireOp",EDGE,"E161.MirrorCS")}),-1.0]])]});
            var Q61;
            Q61=makeQuery(id+"F0.imprint","IMPRINT",FACE,{"disambiguationData":[TD([[makeQuery(id+"F0.imprint","IMPRINT",EDGE,{"derivedFrom":sQuery(id+"F0.wireOp",EDGE,"E10.bottom")}),-1.0]])]});
            var Q62;
            Q62=makeQuery(id+"F0.imprint","IMPRINT",FACE,{"disambiguationData":[TD([[makeQuery(id+"F0.imprint","IMPRINT",EDGE,{"derivedFrom":sQuery(id+"F0.wireOp",EDGE,"E31.MirrorCS")}),1.0]])]});
            var Q63;
            Q63=makeQuery(id+"F0.imprint","IMPRINT",FACE,{"disambiguationData":[TD([[makeQuery(id+"F0.imprint","IMPRINT",EDGE,{"derivedFrom":sQuery(id+"F0.wireOp",EDGE,"E172.MirrorCS")}),-1.0]])]});
            extrude(context, id + "F1", {"entities" : qUnion([Q0, Q1, Q2, Q3, Q4, Q5, Q6, Q7, Q8, Q9, Q10, Q11, Q12, Q13, Q14, Q15, Q16, Q17, Q18, Q19, Q20, Q21, Q22, Q23, Q24, Q25, Q26, Q27, Q28, Q29, Q30, Q31, Q32, Q33, Q34, Q35, Q36, Q37, Q38, Q39, Q40, Q41, Q42, Q43, Q44, Q45, Q46, Q47, Q48, Q49, Q50, Q51, Q52, Q53, Q54, Q55, Q56, Q57, Q58, Q59, Q60, Q61, Q62, Q63]), "depth" : 25.4 * mm, "offsetDistance" : 25.4 * mm});
        }
        {
            var Q0;
            {var subQ2=sQuery(id+"F0.wireOp",EDGE,"E1.bottom");Q0=makeQuery(id+"F0.imprint","IMPRINT",FACE,{"disambiguationData":[TD([[makeQuery(id+"F0.imprint","IMPRINT",EDGE,{"derivedFrom":subQ2}),1.0]])]});}
            var Q1;
            {var subQ32=sQuery(id+"F0.wireOp",EDGE,"E1.top");Q1=makeQuery(id+"F0.imprint","IMPRINT",FACE,{"disambiguationData":[TD([[makeQuery(id+"F0.imprint","IMPRINT",EDGE,{"derivedFrom":subQ32}),-1.0]])]});}
            extrude(context, id + "F2", {"entities" : qUnion([Q0, Q1]), "depth" : 22.22 * mm, "offsetDistance" : 25.4 * mm});
        }
        {
            var Q0;
            Q0=makeQuery(id+"F1.opExtrude","CAP_FACE",FACE,{"disambiguationData":[OSD([sQuery(id+"F0.wireOp",EDGE,"E1.bottom"),sQuery(id+"F0.wireOp",EDGE,"E1.top"),sQuery(id+"F0.wireOp",EDGE,"E1.left"),sQuery(id+"F0.wireOp",EDGE,"E1.right")])],"isStart":false});
            var Q1;
            Q1=makeQuery(id+"F1.opExtrude","CAP_FACE",FACE,{"disambiguationData":[OSD([sQuery(id+"F0.wireOp",EDGE,"E2.bottom"),sQuery(id+"F0.wireOp",EDGE,"E2.top"),sQuery(id+"F0.wireOp",EDGE,"E2.left"),sQuery(id+"F0.wireOp",EDGE,"E2.right")])],"isStart":false});
            var Q2;
            Q2=makeQuery(id+"F1.opExtrude","CAP_FACE",FACE,{"disambiguationData":[OSD([sQuery(id+"F0.wireOp",EDGE,"E4.bottom"),sQuery(id+"F0.wireOp",EDGE,"E4.top"),sQuery(id+"F0.wireOp",EDGE,"E4.left"),sQuery(id+"F0.wireOp",EDGE,"E4.right")])],"isStart":false});
            var Q3;
            Q3=makeQuery(id+"F1.opExtrude","CAP_FACE",FACE,{"disambiguationData":[OSD([sQuery(id+"F0.wireOp",EDGE,"E12.bottom"),sQuery(id+"F0.wireOp",EDGE,"E12.top"),sQuery(id+"F0.wireOp",EDGE,"E12.left"),sQuery(id+"F0.wireOp",EDGE,"E12.right")])],"isStart":false});
            var Q4;
            Q4=makeQuery(id+"F1.opExtrude","CAP_FACE",FACE,{"disambiguationData":[OSD([sQuery(id+"F0.wireOp",EDGE,"E103.MirrorCS"),sQuery(id+"F0.wireOp",EDGE,"E130.MirrorCS"),sQuery(id+"F0.wireOp",EDGE,"E136.MirrorCS"),sQuery(id+"F0.wireOp",EDGE,"E144.MirrorCS")])],"isStart":false});
            var Q5;
            Q5=makeQuery(id+"F1.opExtrude","CAP_FACE",FACE,{"disambiguationData":[OSD([sQuery(id+"F0.wireOp",EDGE,"E86.MirrorCS"),sQuery(id+"F0.wireOp",EDGE,"E118.MirrorCS"),sQuery(id+"F0.wireOp",EDGE,"E128.MirrorCS"),sQuery(id+"F0.wireOp",EDGE,"E131.MirrorCS")])],"isStart":false});
            var Q6;
            Q6=makeQuery(id+"F1.opExtrude","CAP_FACE",FACE,{"disambiguationData":[OSD([sQuery(id+"F0.wireOp",EDGE,"E88.MirrorCS"),sQuery(id+"F0.wireOp",EDGE,"E95.MirrorCS"),sQuery(id+"F0.wireOp",EDGE,"E101.MirrorCS"),sQuery(id+"F0.wireOp",EDGE,"E124.MirrorCS")])],"isStart":false});
            var Q7;
            Q7=makeQuery(id+"F1.opExtrude","CAP_FACE",FACE,{"disambiguationData":[OSD([sQuery(id+"F0.wireOp",EDGE,"E94.MirrorCS"),sQuery(id+"F0.wireOp",EDGE,"E102.MirrorCS"),sQuery(id+"F0.wireOp",EDGE,"E143.MirrorCS"),sQuery(id+"F0.wireOp",EDGE,"E146.MirrorCS")])],"isStart":false});
            var Q8;
            Q8=makeQuery(id+"F1.opExtrude","CAP_FACE",FACE,{"disambiguationData":[OSD([sQuery(id+"F0.wireOp",EDGE,"E104.MirrorCS"),sQuery(id+"F0.wireOp",EDGE,"E105.MirrorCS"),sQuery(id+"F0.wireOp",EDGE,"E138.MirrorCS"),sQuery(id+"F0.wireOp",EDGE,"E147.MirrorCS")])],"isStart":false});
            var Q9;
            Q9=makeQuery(id+"F1.opExtrude","CAP_FACE",FACE,{"disambiguationData":[OSD([sQuery(id+"F0.wireOp",EDGE,"E84.MirrorCS"),sQuery(id+"F0.wireOp",EDGE,"E98.MirrorCS"),sQuery(id+"F0.wireOp",EDGE,"E109.MirrorCS"),sQuery(id+"F0.wireOp",EDGE,"E125.MirrorCS")])],"isStart":false});
            var Q10;
            Q10=makeQuery(id+"F1.opExtrude","CAP_FACE",FACE,{"disambiguationData":[OSD([sQuery(id+"F0.wireOp",EDGE,"E83.MirrorCS"),sQuery(id+"F0.wireOp",EDGE,"E107.MirrorCS"),sQuery(id+"F0.wireOp",EDGE,"E110.MirrorCS"),sQuery(id+"F0.wireOp",EDGE,"E121.MirrorCS")])],"isStart":false});
            var Q11;
            Q11=makeQuery(id+"F1.opExtrude","CAP_FACE",FACE,{"disambiguationData":[OSD([sQuery(id+"F0.wireOp",EDGE,"E82.MirrorCS"),sQuery(id+"F0.wireOp",EDGE,"E108.MirrorCS"),sQuery(id+"F0.wireOp",EDGE,"E120.MirrorCS"),sQuery(id+"F0.wireOp",EDGE,"E153.MirrorCS")])],"isStart":false});
            var Q12;
            Q12=makeQuery(id+"F1.opExtrude","CAP_FACE",FACE,{"disambiguationData":[OSD([sQuery(id+"F0.wireOp",EDGE,"E11.bottom"),sQuery(id+"F0.wireOp",EDGE,"E11.top"),sQuery(id+"F0.wireOp",EDGE,"E11.left"),sQuery(id+"F0.wireOp",EDGE,"E11.right")])],"isStart":false});
            var Q13;
            Q13=makeQuery(id+"F1.opExtrude","CAP_FACE",FACE,{"disambiguationData":[OSD([sQuery(id+"F0.wireOp",EDGE,"E7.bottom"),sQuery(id+"F0.wireOp",EDGE,"E7.top"),sQuery(id+"F0.wireOp",EDGE,"E7.left"),sQuery(id+"F0.wireOp",EDGE,"E7.right")])],"isStart":false});
            var Q14;
            Q14=makeQuery(id+"F1.opExtrude","CAP_FACE",FACE,{"disambiguationData":[OSD([sQuery(id+"F0.wireOp",EDGE,"E6.bottom"),sQuery(id+"F0.wireOp",EDGE,"E6.top"),sQuery(id+"F0.wireOp",EDGE,"E6.left"),sQuery(id+"F0.wireOp",EDGE,"E6.right")])],"isStart":false});
            var Q15;
            Q15=makeQuery(id+"F1.opExtrude","CAP_FACE",FACE,{"disambiguationData":[OSD([sQuery(id+"F0.wireOp",EDGE,"E3.bottom"),sQuery(id+"F0.wireOp",EDGE,"E3.top"),sQuery(id+"F0.wireOp",EDGE,"E3.left"),sQuery(id+"F0.wireOp",EDGE,"E3.right")])],"isStart":false});
            var Q16;
            Q16=makeQuery(id+"F1.opExtrude","CAP_FACE",FACE,{"disambiguationData":[OSD([sQuery(id+"F0.wireOp",EDGE,"E5.bottom"),sQuery(id+"F0.wireOp",EDGE,"E5.top"),sQuery(id+"F0.wireOp",EDGE,"E5.left"),sQuery(id+"F0.wireOp",EDGE,"E5.right")])],"isStart":false});
            var Q17;
            Q17=makeQuery(id+"F1.opExtrude","CAP_FACE",FACE,{"disambiguationData":[OSD([sQuery(id+"F0.wireOp",EDGE,"E8.bottom"),sQuery(id+"F0.wireOp",EDGE,"E8.top"),sQuery(id+"F0.wireOp",EDGE,"E8.left"),sQuery(id+"F0.wireOp",EDGE,"E8.right")])],"isStart":false});
            var Q18;
            Q18=makeQuery(id+"F1.opExtrude","CAP_FACE",FACE,{"disambiguationData":[OSD([sQuery(id+"F0.wireOp",EDGE,"E9.bottom"),sQuery(id+"F0.wireOp",EDGE,"E9.top"),sQuery(id+"F0.wireOp",EDGE,"E9.left"),sQuery(id+"F0.wireOp",EDGE,"E9.right")])],"isStart":false});
            var Q19;
            Q19=makeQuery(id+"F1.opExtrude","CAP_FACE",FACE,{"disambiguationData":[OSD([sQuery(id+"F0.wireOp",EDGE,"E10.bottom"),sQuery(id+"F0.wireOp",EDGE,"E10.top"),sQuery(id+"F0.wireOp",EDGE,"E10.left"),sQuery(id+"F0.wireOp",EDGE,"E10.right")])],"isStart":false});
            var Q20;
            Q20=makeQuery(id+"F1.opExtrude","CAP_FACE",FACE,{"disambiguationData":[OSD([sQuery(id+"F0.wireOp",EDGE,"E99.MirrorCS"),sQuery(id+"F0.wireOp",EDGE,"E116.MirrorCS"),sQuery(id+"F0.wireOp",EDGE,"E151.MirrorCS"),sQuery(id+"F0.wireOp",EDGE,"E155.MirrorCS")])],"isStart":false});
            var Q21;
            Q21=makeQuery(id+"F1.opExtrude","CAP_FACE",FACE,{"disambiguationData":[OSD([sQuery(id+"F0.wireOp",EDGE,"E81.MirrorCS"),sQuery(id+"F0.wireOp",EDGE,"E89.MirrorCS"),sQuery(id+"F0.wireOp",EDGE,"E114.MirrorCS"),sQuery(id+"F0.wireOp",EDGE,"E156.MirrorCS")])],"isStart":false});
            var Q22;
            Q22=makeQuery(id+"F1.opExtrude","CAP_FACE",FACE,{"disambiguationData":[OSD([sQuery(id+"F0.wireOp",EDGE,"E90.MirrorCS"),sQuery(id+"F0.wireOp",EDGE,"E91.MirrorCS"),sQuery(id+"F0.wireOp",EDGE,"E112.MirrorCS"),sQuery(id+"F0.wireOp",EDGE,"E140.MirrorCS")])],"isStart":false});
            var Q23;
            Q23=makeQuery(id+"F1.opExtrude","CAP_FACE",FACE,{"disambiguationData":[OSD([sQuery(id+"F0.wireOp",EDGE,"E96.MirrorCS"),sQuery(id+"F0.wireOp",EDGE,"E113.MirrorCS"),sQuery(id+"F0.wireOp",EDGE,"E132.MirrorCS"),sQuery(id+"F0.wireOp",EDGE,"E133.MirrorCS")])],"isStart":false});
            var Q24;
            Q24=makeQuery(id+"F1.opExtrude","CAP_FACE",FACE,{"disambiguationData":[OSD([sQuery(id+"F0.wireOp",EDGE,"E13.bottom"),sQuery(id+"F0.wireOp",EDGE,"E13.top"),sQuery(id+"F0.wireOp",EDGE,"E13.left"),sQuery(id+"F0.wireOp",EDGE,"E13.right")])],"isStart":false});
            var Q25;
            Q25=makeQuery(id+"F1.opExtrude","CAP_FACE",FACE,{"disambiguationData":[OSD([sQuery(id+"F0.wireOp",EDGE,"E14.bottom"),sQuery(id+"F0.wireOp",EDGE,"E14.top"),sQuery(id+"F0.wireOp",EDGE,"E14.left"),sQuery(id+"F0.wireOp",EDGE,"E14.right")])],"isStart":false});
            var Q26;
            Q26=makeQuery(id+"F1.opExtrude","CAP_FACE",FACE,{"disambiguationData":[OSD([sQuery(id+"F0.wireOp",EDGE,"E15.bottom"),sQuery(id+"F0.wireOp",EDGE,"E15.top"),sQuery(id+"F0.wireOp",EDGE,"E15.left"),sQuery(id+"F0.wireOp",EDGE,"E15.right")])],"isStart":false});
            var Q27;
            Q27=makeQuery(id+"F1.opExtrude","CAP_FACE",FACE,{"disambiguationData":[OSD([sQuery(id+"F0.wireOp",EDGE,"E16.bottom"),sQuery(id+"F0.wireOp",EDGE,"E16.top"),sQuery(id+"F0.wireOp",EDGE,"E16.left"),sQuery(id+"F0.wireOp",EDGE,"E16.right")])],"isStart":false});
            var Q28;
            Q28=makeQuery(id+"F1.opExtrude","CAP_FACE",FACE,{"disambiguationData":[OSD([sQuery(id+"F0.wireOp",EDGE,"E85.MirrorCS"),sQuery(id+"F0.wireOp",EDGE,"E139.MirrorCS"),sQuery(id+"F0.wireOp",EDGE,"E145.MirrorCS"),sQuery(id+"F0.wireOp",EDGE,"E159.MirrorCS")])],"isStart":false});
            var Q29;
            Q29=makeQuery(id+"F1.opExtrude","CAP_FACE",FACE,{"disambiguationData":[OSD([sQuery(id+"F0.wireOp",EDGE,"E87.MirrorCS"),sQuery(id+"F0.wireOp",EDGE,"E111.MirrorCS"),sQuery(id+"F0.wireOp",EDGE,"E119.MirrorCS"),sQuery(id+"F0.wireOp",EDGE,"E150.MirrorCS")])],"isStart":false});
            var Q30;
            Q30=makeQuery(id+"F1.opExtrude","CAP_FACE",FACE,{"disambiguationData":[OSD([sQuery(id+"F0.wireOp",EDGE,"E100.MirrorCS"),sQuery(id+"F0.wireOp",EDGE,"E106.MirrorCS"),sQuery(id+"F0.wireOp",EDGE,"E117.MirrorCS"),sQuery(id+"F0.wireOp",EDGE,"E142.MirrorCS")])],"isStart":false});
            var Q31;
            Q31=makeQuery(id+"F1.opExtrude","CAP_FACE",FACE,{"disambiguationData":[OSD([sQuery(id+"F0.wireOp",EDGE,"E92.MirrorCS"),sQuery(id+"F0.wireOp",EDGE,"E93.MirrorCS"),sQuery(id+"F0.wireOp",EDGE,"E115.MirrorCS"),sQuery(id+"F0.wireOp",EDGE,"E126.MirrorCS")])],"isStart":false});
            var Q32;
            Q32=makeQuery(id+"F1.opExtrude","CAP_FACE",FACE,{"disambiguationData":[OSD([sQuery(id+"F0.wireOp",EDGE,"E97.MirrorCS"),sQuery(id+"F0.wireOp",EDGE,"E129.MirrorCS"),sQuery(id+"F0.wireOp",EDGE,"E135.MirrorCS"),sQuery(id+"F0.wireOp",EDGE,"E160.MirrorCS")])],"isStart":false});
            var Q33;
            Q33=makeQuery(id+"F1.opExtrude","CAP_FACE",FACE,{"disambiguationData":[OSD([sQuery(id+"F0.wireOp",EDGE,"E176.MirrorCS"),sQuery(id+"F0.wireOp",EDGE,"E181.MirrorCS"),sQuery(id+"F0.wireOp",EDGE,"E192.MirrorCS"),sQuery(id+"F0.wireOp",EDGE,"E197.MirrorCS")])],"isStart":false});
            var Q34;
            Q34=makeQuery(id+"F1.opExtrude","CAP_FACE",FACE,{"disambiguationData":[OSD([sQuery(id+"F0.wireOp",EDGE,"E164.MirrorCS"),sQuery(id+"F0.wireOp",EDGE,"E167.MirrorCS"),sQuery(id+"F0.wireOp",EDGE,"E184.MirrorCS"),sQuery(id+"F0.wireOp",EDGE,"E190.MirrorCS")])],"isStart":false});
            var Q35;
            Q35=makeQuery(id+"F1.opExtrude","CAP_FACE",FACE,{"disambiguationData":[OSD([sQuery(id+"F0.wireOp",EDGE,"E171.MirrorCS"),sQuery(id+"F0.wireOp",EDGE,"E183.MirrorCS"),sQuery(id+"F0.wireOp",EDGE,"E187.MirrorCS"),sQuery(id+"F0.wireOp",EDGE,"E207.MirrorCS")])],"isStart":false});
            var Q36;
            Q36=makeQuery(id+"F1.opExtrude","CAP_FACE",FACE,{"disambiguationData":[OSD([sQuery(id+"F0.wireOp",EDGE,"E172.MirrorCS"),sQuery(id+"F0.wireOp",EDGE,"E195.MirrorCS"),sQuery(id+"F0.wireOp",EDGE,"E198.MirrorCS"),sQuery(id+"F0.wireOp",EDGE,"E202.MirrorCS")])],"isStart":false});
            var Q37;
            Q37=makeQuery(id+"F1.opExtrude","CAP_FACE",FACE,{"disambiguationData":[OSD([sQuery(id+"F0.wireOp",EDGE,"E177.MirrorCS"),sQuery(id+"F0.wireOp",EDGE,"E188.MirrorCS"),sQuery(id+"F0.wireOp",EDGE,"E189.MirrorCS"),sQuery(id+"F0.wireOp",EDGE,"E200.MirrorCS")])],"isStart":false});
            var Q38;
            Q38=makeQuery(id+"F1.opExtrude","CAP_FACE",FACE,{"disambiguationData":[OSD([sQuery(id+"F0.wireOp",EDGE,"E162.MirrorCS"),sQuery(id+"F0.wireOp",EDGE,"E199.MirrorCS"),sQuery(id+"F0.wireOp",EDGE,"E204.MirrorCS"),sQuery(id+"F0.wireOp",EDGE,"E208.MirrorCS")])],"isStart":false});
            var Q39;
            Q39=makeQuery(id+"F1.opExtrude","CAP_FACE",FACE,{"disambiguationData":[OSD([sQuery(id+"F0.wireOp",EDGE,"E148.MirrorCS"),sQuery(id+"F0.wireOp",EDGE,"E152.MirrorCS"),sQuery(id+"F0.wireOp",EDGE,"E157.MirrorCS"),sQuery(id+"F0.wireOp",EDGE,"E158.MirrorCS")])],"isStart":false});
            var Q40;
            Q40=makeQuery(id+"F1.opExtrude","CAP_FACE",FACE,{"disambiguationData":[OSD([sQuery(id+"F0.wireOp",EDGE,"E127.MirrorCS"),sQuery(id+"F0.wireOp",EDGE,"E134.MirrorCS"),sQuery(id+"F0.wireOp",EDGE,"E137.MirrorCS"),sQuery(id+"F0.wireOp",EDGE,"E141.MirrorCS")])],"isStart":false});
            var Q41;
            Q41=makeQuery(id+"F1.opExtrude","CAP_FACE",FACE,{"disambiguationData":[OSD([sQuery(id+"F0.wireOp",EDGE,"E170.MirrorCS"),sQuery(id+"F0.wireOp",EDGE,"E182.MirrorCS"),sQuery(id+"F0.wireOp",EDGE,"E191.MirrorCS"),sQuery(id+"F0.wireOp",EDGE,"E194.MirrorCS")])],"isStart":false});
            var Q42;
            Q42=makeQuery(id+"F1.opExtrude","CAP_FACE",FACE,{"disambiguationData":[OSD([sQuery(id+"F0.wireOp",EDGE,"E175.MirrorCS"),sQuery(id+"F0.wireOp",EDGE,"E186.MirrorCS"),sQuery(id+"F0.wireOp",EDGE,"E193.MirrorCS"),sQuery(id+"F0.wireOp",EDGE,"E206.MirrorCS")])],"isStart":false});
            var Q43;
            Q43=makeQuery(id+"F1.opExtrude","CAP_FACE",FACE,{"disambiguationData":[OSD([sQuery(id+"F0.wireOp",EDGE,"E122.MirrorCS"),sQuery(id+"F0.wireOp",EDGE,"E123.MirrorCS"),sQuery(id+"F0.wireOp",EDGE,"E149.MirrorCS"),sQuery(id+"F0.wireOp",EDGE,"E154.MirrorCS")])],"isStart":false});
            var Q44;
            Q44=makeQuery(id+"F1.opExtrude","CAP_FACE",FACE,{"disambiguationData":[OSD([sQuery(id+"F0.wireOp",EDGE,"E165.MirrorCS"),sQuery(id+"F0.wireOp",EDGE,"E174.MirrorCS"),sQuery(id+"F0.wireOp",EDGE,"E185.MirrorCS"),sQuery(id+"F0.wireOp",EDGE,"E203.MirrorCS")])],"isStart":false});
            var Q45;
            Q45=makeQuery(id+"F1.opExtrude","CAP_FACE",FACE,{"disambiguationData":[OSD([sQuery(id+"F0.wireOp",EDGE,"E168.MirrorCS"),sQuery(id+"F0.wireOp",EDGE,"E178.MirrorCS"),sQuery(id+"F0.wireOp",EDGE,"E196.MirrorCS"),sQuery(id+"F0.wireOp",EDGE,"E205.MirrorCS")])],"isStart":false});
            var Q46;
            Q46=makeQuery(id+"F1.opExtrude","CAP_FACE",FACE,{"disambiguationData":[OSD([sQuery(id+"F0.wireOp",EDGE,"E161.MirrorCS"),sQuery(id+"F0.wireOp",EDGE,"E163.MirrorCS"),sQuery(id+"F0.wireOp",EDGE,"E173.MirrorCS"),sQuery(id+"F0.wireOp",EDGE,"E179.MirrorCS")])],"isStart":false});
            var Q47;
            Q47=makeQuery(id+"F1.opExtrude","CAP_FACE",FACE,{"disambiguationData":[OSD([sQuery(id+"F0.wireOp",EDGE,"E166.MirrorCS"),sQuery(id+"F0.wireOp",EDGE,"E169.MirrorCS"),sQuery(id+"F0.wireOp",EDGE,"E180.MirrorCS"),sQuery(id+"F0.wireOp",EDGE,"E201.MirrorCS")])],"isStart":false});
            var Q48;
            Q48=makeQuery(id+"F1.opExtrude","CAP_FACE",FACE,{"disambiguationData":[OSD([sQuery(id+"F0.wireOp",EDGE,"E31.MirrorCS"),sQuery(id+"F0.wireOp",EDGE,"E50.MirrorCS"),sQuery(id+"F0.wireOp",EDGE,"E60.MirrorCS"),sQuery(id+"F0.wireOp",EDGE,"E78.MirrorCS")])],"isStart":false});
            var Q49;
            Q49=makeQuery(id+"F1.opExtrude","CAP_FACE",FACE,{"disambiguationData":[OSD([sQuery(id+"F0.wireOp",EDGE,"E22.MirrorCS"),sQuery(id+"F0.wireOp",EDGE,"E25.MirrorCS"),sQuery(id+"F0.wireOp",EDGE,"E28.MirrorCS"),sQuery(id+"F0.wireOp",EDGE,"E64.MirrorCS")])],"isStart":false});
            var Q50;
            Q50=makeQuery(id+"F1.opExtrude","CAP_FACE",FACE,{"disambiguationData":[OSD([sQuery(id+"F0.wireOp",EDGE,"E20.MirrorCS"),sQuery(id+"F0.wireOp",EDGE,"E24.MirrorCS"),sQuery(id+"F0.wireOp",EDGE,"E65.MirrorCS"),sQuery(id+"F0.wireOp",EDGE,"E71.MirrorCS")])],"isStart":false});
            var Q51;
            Q51=makeQuery(id+"F1.opExtrude","CAP_FACE",FACE,{"disambiguationData":[OSD([sQuery(id+"F0.wireOp",EDGE,"E35.MirrorCS"),sQuery(id+"F0.wireOp",EDGE,"E49.MirrorCS"),sQuery(id+"F0.wireOp",EDGE,"E58.MirrorCS"),sQuery(id+"F0.wireOp",EDGE,"E70.MirrorCS")])],"isStart":false});
            var Q52;
            Q52=makeQuery(id+"F1.opExtrude","CAP_FACE",FACE,{"disambiguationData":[OSD([sQuery(id+"F0.wireOp",EDGE,"E17.MirrorCS"),sQuery(id+"F0.wireOp",EDGE,"E23.MirrorCS"),sQuery(id+"F0.wireOp",EDGE,"E46.MirrorCS"),sQuery(id+"F0.wireOp",EDGE,"E54.MirrorCS")])],"isStart":false});
            var Q53;
            Q53=makeQuery(id+"F1.opExtrude","CAP_FACE",FACE,{"disambiguationData":[OSD([sQuery(id+"F0.wireOp",EDGE,"E32.MirrorCS"),sQuery(id+"F0.wireOp",EDGE,"E42.MirrorCS"),sQuery(id+"F0.wireOp",EDGE,"E66.MirrorCS"),sQuery(id+"F0.wireOp",EDGE,"E72.MirrorCS")])],"isStart":false});
            var Q54;
            Q54=makeQuery(id+"F1.opExtrude","CAP_FACE",FACE,{"disambiguationData":[OSD([sQuery(id+"F0.wireOp",EDGE,"E39.MirrorCS"),sQuery(id+"F0.wireOp",EDGE,"E56.MirrorCS"),sQuery(id+"F0.wireOp",EDGE,"E63.MirrorCS"),sQuery(id+"F0.wireOp",EDGE,"E79.MirrorCS")])],"isStart":false});
            var Q55;
            Q55=makeQuery(id+"F1.opExtrude","CAP_FACE",FACE,{"disambiguationData":[OSD([sQuery(id+"F0.wireOp",EDGE,"E18.MirrorCS"),sQuery(id+"F0.wireOp",EDGE,"E19.MirrorCS"),sQuery(id+"F0.wireOp",EDGE,"E30.MirrorCS"),sQuery(id+"F0.wireOp",EDGE,"E77.MirrorCS")])],"isStart":false});
            var Q56;
            Q56=makeQuery(id+"F1.opExtrude","CAP_FACE",FACE,{"disambiguationData":[OSD([sQuery(id+"F0.wireOp",EDGE,"E29.MirrorCS"),sQuery(id+"F0.wireOp",EDGE,"E57.MirrorCS"),sQuery(id+"F0.wireOp",EDGE,"E74.MirrorCS"),sQuery(id+"F0.wireOp",EDGE,"E80.MirrorCS")])],"isStart":false});
            var Q57;
            Q57=makeQuery(id+"F1.opExtrude","CAP_FACE",FACE,{"disambiguationData":[OSD([sQuery(id+"F0.wireOp",EDGE,"E38.MirrorCS"),sQuery(id+"F0.wireOp",EDGE,"E40.MirrorCS"),sQuery(id+"F0.wireOp",EDGE,"E47.MirrorCS"),sQuery(id+"F0.wireOp",EDGE,"E51.MirrorCS")])],"isStart":false});
            var Q58;
            Q58=makeQuery(id+"F1.opExtrude","CAP_FACE",FACE,{"disambiguationData":[OSD([sQuery(id+"F0.wireOp",EDGE,"E43.MirrorCS"),sQuery(id+"F0.wireOp",EDGE,"E44.MirrorCS"),sQuery(id+"F0.wireOp",EDGE,"E61.MirrorCS"),sQuery(id+"F0.wireOp",EDGE,"E62.MirrorCS")])],"isStart":false});
            var Q59;
            Q59=makeQuery(id+"F1.opExtrude","CAP_FACE",FACE,{"disambiguationData":[OSD([sQuery(id+"F0.wireOp",EDGE,"E48.MirrorCS"),sQuery(id+"F0.wireOp",EDGE,"E52.MirrorCS"),sQuery(id+"F0.wireOp",EDGE,"E67.MirrorCS"),sQuery(id+"F0.wireOp",EDGE,"E75.MirrorCS")])],"isStart":false});
            var Q60;
            Q60=makeQuery(id+"F1.opExtrude","CAP_FACE",FACE,{"disambiguationData":[OSD([sQuery(id+"F0.wireOp",EDGE,"E27.MirrorCS"),sQuery(id+"F0.wireOp",EDGE,"E36.MirrorCS"),sQuery(id+"F0.wireOp",EDGE,"E37.MirrorCS"),sQuery(id+"F0.wireOp",EDGE,"E53.MirrorCS")])],"isStart":false});
            var Q61;
            Q61=makeQuery(id+"F1.opExtrude","CAP_FACE",FACE,{"disambiguationData":[OSD([sQuery(id+"F0.wireOp",EDGE,"E21.MirrorCS"),sQuery(id+"F0.wireOp",EDGE,"E41.MirrorCS"),sQuery(id+"F0.wireOp",EDGE,"E55.MirrorCS"),sQuery(id+"F0.wireOp",EDGE,"E68.MirrorCS")])],"isStart":false});
            var Q62;
            Q62=makeQuery(id+"F1.opExtrude","CAP_FACE",FACE,{"disambiguationData":[OSD([sQuery(id+"F0.wireOp",EDGE,"E26.MirrorCS"),sQuery(id+"F0.wireOp",EDGE,"E34.MirrorCS"),sQuery(id+"F0.wireOp",EDGE,"E59.MirrorCS"),sQuery(id+"F0.wireOp",EDGE,"E76.MirrorCS")])],"isStart":false});
            var Q63;
            Q63=makeQuery(id+"F1.opExtrude","CAP_FACE",FACE,{"disambiguationData":[OSD([sQuery(id+"F0.wireOp",EDGE,"E33.MirrorCS"),sQuery(id+"F0.wireOp",EDGE,"E45.MirrorCS"),sQuery(id+"F0.wireOp",EDGE,"E69.MirrorCS"),sQuery(id+"F0.wireOp",EDGE,"E73.MirrorCS")])],"isStart":false});
            chamfer(context, id + "F3", {"entities" : qUnion([Q0, Q1, Q2, Q3, Q4, Q5, Q6, Q7, Q8, Q9, Q10, Q11, Q12, Q13, Q14, Q15, Q16, Q17, Q18, Q19, Q20, Q21, Q22, Q23, Q24, Q25, Q26, Q27, Q28, Q29, Q30, Q31, Q32, Q33, Q34, Q35, Q36, Q37, Q38, Q39, Q40, Q41, Q42, Q43, Q44, Q45, Q46, Q47, Q48, Q49, Q50, Q51, Q52, Q53, Q54, Q55, Q56, Q57, Q58, Q59, Q60, Q61, Q62, Q63]), "width" : 3.17 * mm, "tangentPropagation" : true});
        }
    });
